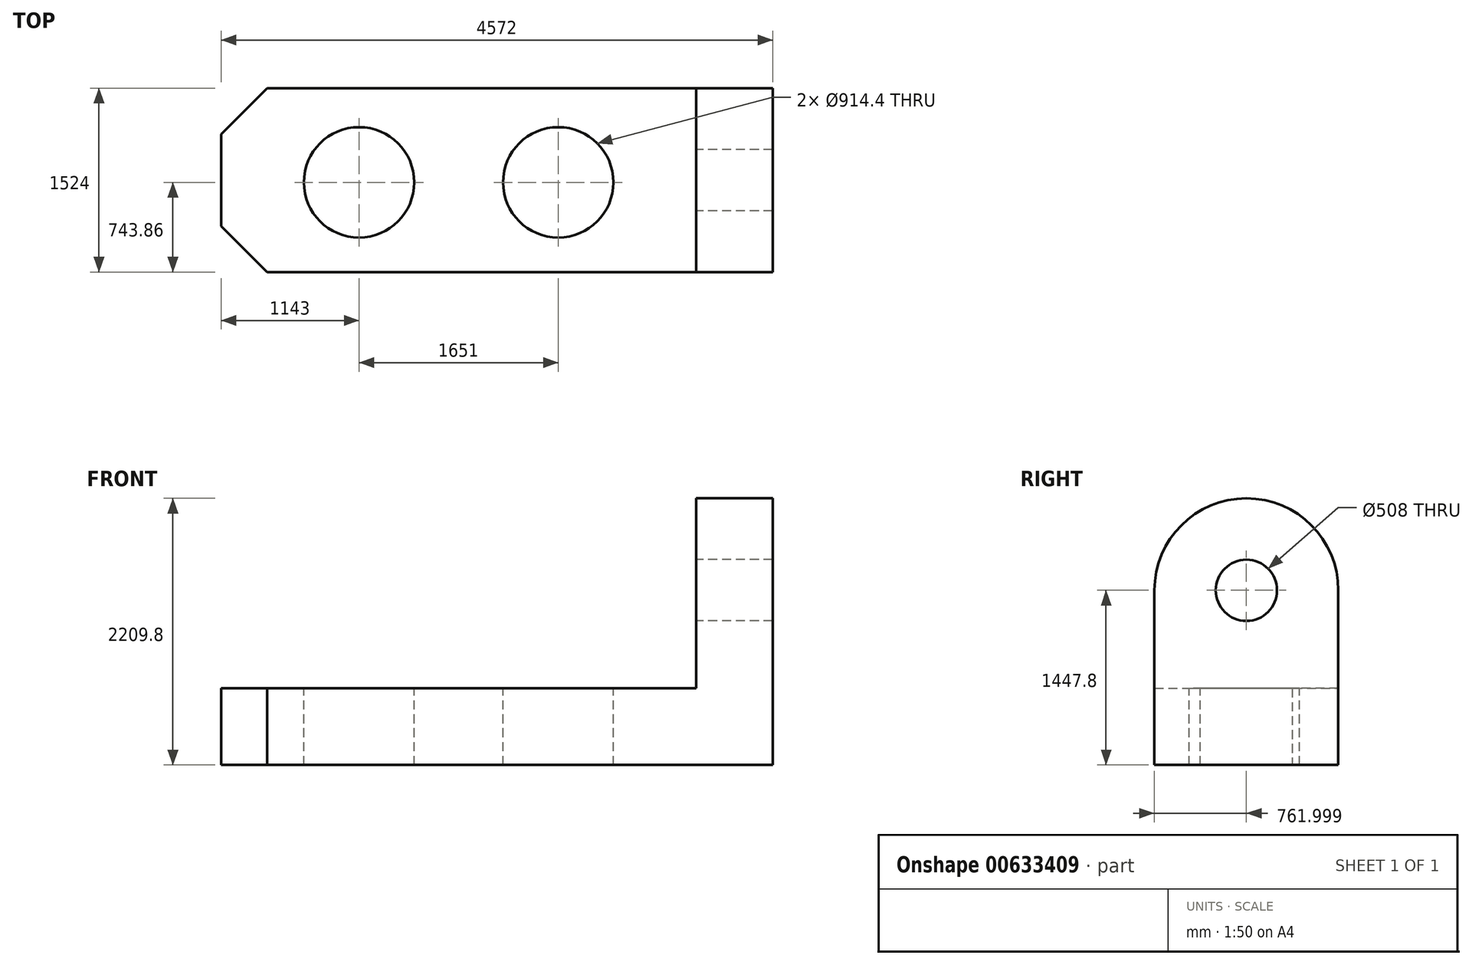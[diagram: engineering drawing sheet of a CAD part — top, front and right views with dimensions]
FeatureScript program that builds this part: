
annotation { "Feature Type Name" : "Feature", "Feature Type Description" : "" }
export const myFeature = defineFeature(function(context is Context, id is Id, definition is map)
    precondition{}
    {
        {
            var Q0;
            Q0=qCreatedBy(makeId("Top.planeOp"),FACE);
            var sketch = newSketch(context, id + "F0", { "sketchPlane" : qUnion([Q0])});
            skLineSegment(sketch, "E0.bottom", {"start": v(-2287.04, 780.14) * mm, "end": v(2284.96, 780.14) * mm});
            skLineSegment(sketch, "E0.top", {"start": v(-2287.04, -743.86) * mm, "end": v(2284.96, -743.86) * mm});
            skLineSegment(sketch, "E0.left", {"start": v(-2287.04, 780.14) * mm, "end": v(-2287.04, -743.86) * mm});
            skLineSegment(sketch, "E0.right", {"start": v(2284.96, 780.14) * mm, "end": v(2284.96, -743.86) * mm});
            skSolve(sketch);
        }
        {
            var Q0;
            Q0 = qSketchRegion(id + "F0", true);
            extrude(context, id + "F1", {"entities" : qUnion([Q0]), "depth" : 635 * mm, "offsetDistance" : 25.4 * mm});
        }
        {
            var Q0;
            Q0=makeQuery(id+"F1.opExtrude","CAP_FACE",FACE,{"disambiguationData":[OSD([sQuery(id+"F0.wireOp",EDGE,"E0.bottom"),sQuery(id+"F0.wireOp",EDGE,"E0.top"),sQuery(id+"F0.wireOp",EDGE,"E0.left"),sQuery(id+"F0.wireOp",EDGE,"E0.right")])],"isStart":false});
            var sketch = newSketch(context, id + "F2", { "sketchPlane" : qUnion([Q0])});
            skLineSegment(sketch, "E1.bottom", {"start": v(2284.96, -743.86) * mm, "end": v(1649.66, -743.86) * mm});
            skLineSegment(sketch, "E1.top", {"start": v(2284.96, 780.14) * mm, "end": v(1649.66, 780.14) * mm});
            skLineSegment(sketch, "E1.left", {"start": v(2284.96, -743.86) * mm, "end": v(2284.96, 780.14) * mm});
            skLineSegment(sketch, "E1.right", {"start": v(1649.66, -743.86) * mm, "end": v(1649.66, 780.14) * mm});
            skSolve(sketch);
        }
        {
            var Q0;
            Q0=makeQuery(id+"F2.imprint","IMPRINT",FACE,{"disambiguationData":[TD([[makeQuery(id+"F2.imprint","IMPRINT",EDGE,{"derivedFrom":sQuery(id+"F2.wireOp",EDGE,"E1.bottom")}),1.0]])]});
            extrude(context, id + "F3", {"entities" : qUnion([Q0]), "operationType" : NewBodyOperationType.ADD, "depth" : 1574.8 * mm, "offsetDistance" : 25.4 * mm});
        }
        {
            var Q0;
            Q0=makeQuery(id+"F3.opExtrude","CAP_EDGE",EDGE,{"disambiguationData":[OSD([sQuery(id+"F2.wireOp",EDGE,"E1.top")])],"isStart":false});
            var Q1;
            Q1=makeQuery(id+"F3.opExtrude","CAP_EDGE",EDGE,{"disambiguationData":[OSD([sQuery(id+"F2.wireOp",EDGE,"E1.bottom")])],"isStart":false});
            fillet(context, id + "F4", {"entities" : qUnion([Q0, Q1]), "radius" : 762 * mm, "tangentPropagation" : true, "allowEdgeOverflow" : false});
        }
        {
            var Q0;
            Q0=makeQuery(id+"F1.opExtrude","CAP_FACE",FACE,{"disambiguationData":[OSD([sQuery(id+"F0.wireOp",EDGE,"E0.bottom"),sQuery(id+"F0.wireOp",EDGE,"E0.top"),sQuery(id+"F0.wireOp",EDGE,"E0.left"),sQuery(id+"F0.wireOp",EDGE,"E0.right")])],"isStart":false});
            var sketch = newSketch(context, id + "F5", { "sketchPlane" : qUnion([Q0])});
            skCircle(sketch, "E2", {"center": v(506.96, 0) * mm, "radius": 457.2 * mm});
            skCircle(sketch, "E3", {"center": v(-1144.04, 0) * mm, "radius": 457.2 * mm});
            skSolve(sketch);
        }
        {
            var Q0;
            Q0=makeQuery(id+"F5.imprint","IMPRINT",FACE,{"disambiguationData":[TD([[makeQuery(id+"F5.imprint","IMPRINT",EDGE,{"derivedFrom":sQuery(id+"F5.wireOp",EDGE,"E3")}),1.0]])]});
            var Q1;
            Q1=makeQuery(id+"F5.imprint","IMPRINT",FACE,{"disambiguationData":[TD([[makeQuery(id+"F5.imprint","IMPRINT",EDGE,{"derivedFrom":sQuery(id+"F5.wireOp",EDGE,"E2")}),1.0]])]});
            extrude(context, id + "F6", {"entities" : qUnion([Q0, Q1]), "operationType" : NewBodyOperationType.REMOVE, "oppositeDirection" : true, "depth" : 889 * mm, "offsetDistance" : 25.4 * mm});
        }
        {
            var Q0;
            Q0=makeQuery(id+"F3.opExtrude","SWEPT_FACE",FACE,{"disambiguationData":[OSD([sQuery(id+"F2.wireOp",EDGE,"E1.right")])]});
            var sketch = newSketch(context, id + "F7", { "sketchPlane" : qUnion([Q0])});
            skCircle(sketch, "E4", {"center": v(-18.14, 1447.8) * mm, "radius": 254 * mm});
            skSolve(sketch);
        }
        {
            var Q0;
            Q0=makeQuery(id+"F7.imprint","IMPRINT",FACE,{"disambiguationData":[TD([[makeQuery(id+"F7.imprint","IMPRINT",EDGE,{"derivedFrom":sQuery(id+"F7.wireOp",EDGE,"E4")}),1.0]])]});
            extrude(context, id + "F8", {"entities" : qUnion([Q0]), "operationType" : NewBodyOperationType.REMOVE, "oppositeDirection" : true, "depth" : 635 * mm, "offsetDistance" : 25.4 * mm});
        }
        {
            var Q0;
            Q0=makeQuery(id+"F8.boolean.opBoolean","COPY",FACE,{"derivedFrom":makeQuery(id+"F8.opExtrude","CAP_FACE",FACE,{"disambiguationData":[OSD([sQuery(id+"F7.wireOp",EDGE,"E4")])],"isStart":false})});
            extrude(context, id + "F9", {"entities" : qUnion([Q0]), "operationType" : NewBodyOperationType.REMOVE, "oppositeDirection" : true, "depth" : 25.4 * mm, "offsetDistance" : 25.4 * mm});
        }
        {
            var Q0;
            Q0=makeQuery(id+"F1.opExtrude","SWEPT_EDGE",EDGE,{"disambiguationData":[OSD([sQuery(id+"F0.wireOp",EDGE,"E0.top"),sQuery(id+"F0.wireOp",EDGE,"E0.left")])]});
            var Q1;
            Q1=makeQuery(id+"F1.opExtrude","SWEPT_EDGE",EDGE,{"disambiguationData":[OSD([sQuery(id+"F0.wireOp",EDGE,"E0.bottom"),sQuery(id+"F0.wireOp",EDGE,"E0.left")])]});
            chamfer(context, id + "F10", {"entities" : qUnion([Q0, Q1]), "width" : 381 * mm, "tangentPropagation" : true});
        }
    });
